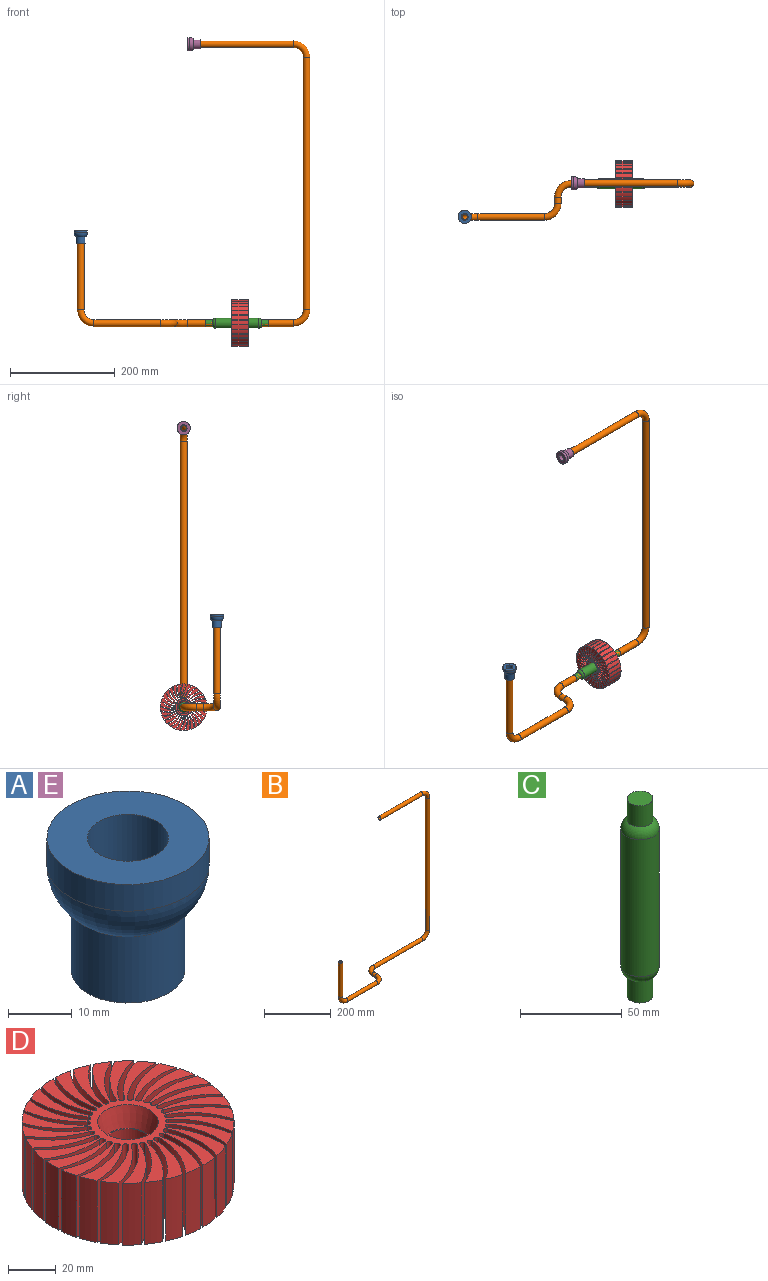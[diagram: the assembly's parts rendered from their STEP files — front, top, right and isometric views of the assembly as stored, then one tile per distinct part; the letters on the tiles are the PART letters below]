
ASSEMBLY  parts=5 mates=4
PART A: 6 faces, bbox 25.4x25.4x25.4 mm
  f0: plane 17.78x17.78mm, normal (0,0,-1), area 121.6mm2, adj f1,f5
  f1: cylinder r=6.35mm len=25.4mm, axis (0,0,-1), area 1013.4mm2, adj f0,f2
  f2: plane 25.4x25.4mm, normal (0,0,1), area 380mm2, adj f1,f3
  f3: cylinder r=12.7mm len=25.4mm, axis (0,0,-1), area 405.4mm2, adj f2,f4
  f4: torus R=3.17mm, axis (0,0,-1), area 632.2mm2, adj f3,f5
  f5: cylinder r=8.89mm len=17.78mm, axis (0,0,-1), area 709.4mm2, adj f0,f4
PART B: 24 faces, bbox 449.7x81.4x551.3 mm
  f0: cylinder r=4.91mm len=127mm, axis (0,0,-1), area 3916.4mm2, adj f1,f11
  f1: torus R=25.4mm, axis (0,-1,0), area 1230.4mm2, adj f0,f2
  f2: cylinder r=4.91mm len=127mm, axis (1,0,0), area 3916.4mm2, adj f1,f3
  f3: torus R=25.4mm, axis (0,0,1), area 1230.4mm2, adj f2,f4
  f4: cylinder r=4.91mm len=12.7mm, axis (0,1,0), area 391.6mm2, adj f3,f5
  f5: torus R=25.4mm, axis (0,0,-1), area 1230.4mm2, adj f4,f6
  f6: cylinder r=4.91mm len=203.2mm, axis (1,0,0), area 6266.3mm2, adj f5,f7
  f7: torus R=25.4mm, axis (0,-1,0), area 1230.4mm2, adj f6,f8
  f8: cylinder r=4.91mm len=482.6mm, axis (0,0,1), area 14882.4mm2, adj f7,f9
  f9: torus R=25.4mm, axis (0,-1,0), area 1230.4mm2, adj f8,f10
  f10: cylinder r=4.91mm len=177.8mm, axis (-1,0,0), area 5483mm2, adj f9,f12
  f11: plane 12.7x12.7mm, normal (0,0,1), area 51mm2, adj f0,f13
  f12: plane 12.7x12.7mm, normal (-1,0,0), area 51mm2, adj f10,f23
  f13: cylinder r=6.35mm len=127mm, axis (0,0,-1), area 5067.1mm2, adj f11,f14
  f14: torus R=25.4mm, axis (0,-1,0), area 1591.9mm2, adj f13,f15
  f15: cylinder r=6.35mm len=127mm, axis (1,0,0), area 5067.1mm2, adj f14,f16
  f16: torus R=25.4mm, axis (0,0,1), area 1591.9mm2, adj f15,f17
  f17: cylinder r=6.35mm len=12.7mm, axis (0,1,0), area 506.7mm2, adj f16,f18
  f18: torus R=25.4mm, axis (0,0,-1), area 1591.9mm2, adj f17,f19
  f19: cylinder r=6.35mm len=203.2mm, axis (1,0,0), area 8107.3mm2, adj f18,f20
  f20: torus R=25.4mm, axis (0,-1,0), area 1591.9mm2, adj f19,f21
  f21: cylinder r=6.35mm len=482.6mm, axis (0,0,1), area 19254.9mm2, adj f20,f22
  f22: torus R=25.4mm, axis (0,-1,0), area 1591.9mm2, adj f21,f23
  f23: cylinder r=6.35mm len=177.8mm, axis (-1,0,0), area 7093.9mm2, adj f12,f22
PART C: 7 faces, bbox 19.1x19.1x118.8 mm
  f0: cylinder r=9.53mm len=82.55mm, axis (0,0,-1), area 4940.4mm2, adj f3,f6
  f1: plane 12.7x12.7mm, normal (0,0,1), area 126.7mm2, adj f2
  f2: cylinder r=6.35mm len=12.7mm, axis (0,0,-1), area 506.7mm2, adj f1,f3
  f3: torus R=3.31mm, axis (0,0,-1), area 348.8mm2, adj f0,f2
  f4: plane 12.7x12.7mm, normal (0,0,-1), area 126.7mm2, adj f5
  f5: cylinder r=6.35mm len=12.7mm, axis (0,0,1), area 506.7mm2, adj f4,f6
  f6: torus R=3.31mm, axis (0,0,1), area 348.8mm2, adj f0,f5
PART D: 125 faces, bbox 88.9x88.9x31.8 mm
  f0: cylinder r=44.45mm len=31.75mm, axis (0,0,-1), area 250.2mm2, adj f1,f117,f118,f124
  f1: cylinder r=38.1mm len=31.75mm, axis (0,0,1), area 922.7mm2, adj f0,f2,f117,f118
  f2: cylinder r=1.27mm len=31.75mm, axis (0,0,1), area 126.7mm2, adj f1,f3,f117,f118
  f3: cylinder r=40.64mm len=31.75mm, axis (0,0,1), area 895.9mm2, adj f2,f4,f117,f118
  f4: cylinder r=44.45mm len=31.75mm, axis (0,0,-1), area 250.2mm2, adj f3,f5,f117,f118
  f5: cylinder r=38.1mm len=31.75mm, axis (0,0,1), area 922.7mm2, adj f4,f6,f117,f118
  f6: cylinder r=1.27mm len=31.75mm, axis (0,0,1), area 126.7mm2, adj f5,f7,f117,f118
  f7: cylinder r=40.64mm len=31.75mm, axis (0,0,1), area 895.9mm2, adj f6,f8,f117,f118
  f8: cylinder r=44.45mm len=31.75mm, axis (0,0,-1), area 250.2mm2, adj f7,f9,f117,f118
  f9: cylinder r=38.1mm len=31.75mm, axis (0,0,1), area 922.7mm2, adj f8,f10,f117,f118
  f10: cylinder r=1.27mm len=31.75mm, axis (0,0,1), area 126.7mm2, adj f9,f11,f117,f118
  f11: cylinder r=40.64mm len=31.75mm, axis (0,0,1), area 895.9mm2, adj f10,f12,f117,f118
  f12: cylinder r=44.45mm len=31.75mm, axis (0,0,-1), area 250.2mm2, adj f11,f13,f117,f118
  f13: cylinder r=38.1mm len=31.75mm, axis (0,0,1), area 922.7mm2, adj f12,f14,f117,f118
  f14: cylinder r=1.27mm len=31.75mm, axis (0,0,1), area 126.7mm2, adj f13,f15,f117,f118
  f15: cylinder r=40.64mm len=31.75mm, axis (0,0,1), area 895.9mm2, adj f14,f16,f117,f118
  f16: cylinder r=44.45mm len=31.75mm, axis (0,0,-1), area 250.2mm2, adj f15,f17,f117,f118
  f17: cylinder r=38.1mm len=31.75mm, axis (0,0,1), area 922.7mm2, adj f16,f18,f117,f118
  f18: cylinder r=1.27mm len=31.75mm, axis (0,0,1), area 126.7mm2, adj f17,f19,f117,f118
  f19: cylinder r=40.64mm len=31.75mm, axis (0,0,1), area 895.9mm2, adj f18,f20,f117,f118
  f20: cylinder r=44.45mm len=31.75mm, axis (0,0,-1), area 250.2mm2, adj f19,f21,f117,f118
  f21: cylinder r=38.1mm len=31.75mm, axis (0,0,1), area 922.7mm2, adj f20,f22,f117,f118
  f22: cylinder r=1.27mm len=31.75mm, axis (0,0,1), area 126.7mm2, adj f21,f23,f117,f118
  f23: cylinder r=40.64mm len=31.75mm, axis (0,0,1), area 895.9mm2, adj f22,f24,f117,f118
  f24: cylinder r=44.45mm len=31.75mm, axis (0,0,-1), area 250.2mm2, adj f23,f25,f117,f118
  f25: cylinder r=38.1mm len=31.75mm, axis (0,0,1), area 922.7mm2, adj f24,f26,f117,f118
  f26: cylinder r=1.27mm len=31.75mm, axis (0,0,1), area 126.7mm2, adj f25,f27,f117,f118
  f27: cylinder r=40.64mm len=31.75mm, axis (0,0,1), area 895.9mm2, adj f26,f28,f117,f118
  f28: cylinder r=44.45mm len=31.75mm, axis (0,0,-1), area 250.2mm2, adj f27,f29,f117,f118
  f29: cylinder r=38.1mm len=31.75mm, axis (0,0,1), area 922.7mm2, adj f28,f30,f117,f118
  f30: cylinder r=1.27mm len=31.75mm, axis (0,0,1), area 126.7mm2, adj f29,f31,f117,f118
  f31: cylinder r=40.64mm len=31.75mm, axis (0,0,1), area 895.9mm2, adj f30,f32,f117,f118
  f32: cylinder r=44.45mm len=31.75mm, axis (0,0,-1), area 250.2mm2, adj f31,f33,f117,f118
  f33: cylinder r=38.1mm len=31.75mm, axis (0,0,1), area 922.7mm2, adj f32,f34,f117,f118
  f34: cylinder r=1.27mm len=31.75mm, axis (0,0,1), area 126.7mm2, adj f33,f35,f117,f118
  f35: cylinder r=40.64mm len=31.75mm, axis (0,0,1), area 895.9mm2, adj f34,f36,f117,f118
  f36: cylinder r=44.45mm len=31.75mm, axis (0,0,-1), area 250.2mm2, adj f35,f37,f117,f118
  f37: cylinder r=38.1mm len=31.75mm, axis (0,0,1), area 922.7mm2, adj f36,f38,f117,f118
  f38: cylinder r=1.27mm len=31.75mm, axis (0,0,1), area 126.7mm2, adj f37,f39,f117,f118
  f39: cylinder r=40.64mm len=31.75mm, axis (0,0,1), area 895.9mm2, adj f38,f40,f117,f118
  f40: cylinder r=44.45mm len=31.75mm, axis (0,0,-1), area 250.2mm2, adj f39,f41,f117,f118
  f41: cylinder r=38.1mm len=31.75mm, axis (0,0,1), area 922.7mm2, adj f40,f42,f117,f118
  f42: cylinder r=1.27mm len=31.75mm, axis (0,0,1), area 126.7mm2, adj f41,f43,f117,f118
  f43: cylinder r=40.64mm len=31.75mm, axis (0,0,1), area 895.9mm2, adj f42,f44,f117,f118
  f44: cylinder r=44.45mm len=31.75mm, axis (0,0,-1), area 250.2mm2, adj f43,f45,f117,f118
  f45: cylinder r=38.1mm len=31.75mm, axis (0,0,1), area 922.7mm2, adj f44,f46,f117,f118
  f46: cylinder r=1.27mm len=31.75mm, axis (0,0,1), area 126.7mm2, adj f45,f47,f117,f118
  f47: cylinder r=40.64mm len=31.75mm, axis (0,0,1), area 895.9mm2, adj f46,f48,f117,f118
  f48: cylinder r=44.45mm len=31.75mm, axis (0,0,-1), area 250.2mm2, adj f47,f49,f117,f118
  f49: cylinder r=38.1mm len=31.75mm, axis (0,0,1), area 922.7mm2, adj f48,f50,f117,f118
  f50: cylinder r=1.27mm len=31.75mm, axis (0,0,1), area 126.7mm2, adj f49,f51,f117,f118
  f51: cylinder r=40.64mm len=31.75mm, axis (0,0,1), area 895.9mm2, adj f50,f52,f117,f118
  f52: cylinder r=44.45mm len=31.75mm, axis (0,0,-1), area 250.2mm2, adj f51,f53,f117,f118
  f53: cylinder r=38.1mm len=31.75mm, axis (0,0,1), area 922.7mm2, adj f52,f54,f117,f118
  f54: cylinder r=1.27mm len=31.75mm, axis (0,0,1), area 126.7mm2, adj f53,f55,f117,f118
  f55: cylinder r=40.64mm len=31.75mm, axis (0,0,1), area 895.9mm2, adj f54,f56,f117,f118
  f56: cylinder r=44.45mm len=31.75mm, axis (0,0,-1), area 250.2mm2, adj f55,f57,f117,f118
  f57: cylinder r=38.1mm len=31.75mm, axis (0,0,1), area 922.7mm2, adj f56,f58,f117,f118
  f58: cylinder r=1.27mm len=31.75mm, axis (0,0,1), area 126.7mm2, adj f57,f59,f117,f118
  f59: cylinder r=40.64mm len=31.75mm, axis (0,0,1), area 895.9mm2, adj f58,f60,f117,f118
  f60: cylinder r=44.45mm len=31.75mm, axis (0,0,-1), area 250.2mm2, adj f59,f61,f117,f118
  f61: cylinder r=38.1mm len=31.75mm, axis (0,0,1), area 922.7mm2, adj f60,f62,f117,f118
  f62: cylinder r=1.27mm len=31.75mm, axis (0,0,1), area 126.7mm2, adj f61,f63,f117,f118
  f63: cylinder r=40.64mm len=31.75mm, axis (0,0,1), area 895.9mm2, adj f62,f64,f117,f118
  f64: cylinder r=44.45mm len=31.75mm, axis (0,0,-1), area 250.2mm2, adj f63,f65,f117,f118
  f65: cylinder r=38.1mm len=31.75mm, axis (0,0,1), area 922.7mm2, adj f64,f66,f117,f118
  f66: cylinder r=1.27mm len=31.75mm, axis (0,0,1), area 126.7mm2, adj f65,f67,f117,f118
  f67: cylinder r=40.64mm len=31.75mm, axis (0,0,1), area 895.9mm2, adj f66,f68,f117,f118
  f68: cylinder r=44.45mm len=31.75mm, axis (0,0,-1), area 250.2mm2, adj f67,f69,f117,f118
  f69: cylinder r=38.1mm len=31.75mm, axis (0,0,1), area 922.7mm2, adj f68,f70,f117,f118
  f70: cylinder r=1.27mm len=31.75mm, axis (0,0,1), area 126.7mm2, adj f69,f71,f117,f118
  f71: cylinder r=40.64mm len=31.75mm, axis (0,0,1), area 895.9mm2, adj f70,f72,f117,f118
  f72: cylinder r=44.45mm len=31.75mm, axis (0,0,-1), area 250.2mm2, adj f71,f73,f117,f118
  f73: cylinder r=38.1mm len=31.75mm, axis (0,0,1), area 922.7mm2, adj f72,f74,f117,f118
  f74: cylinder r=1.27mm len=31.75mm, axis (0,0,1), area 126.7mm2, adj f73,f75,f117,f118
  f75: cylinder r=40.64mm len=31.75mm, axis (0,0,1), area 895.9mm2, adj f74,f76,f117,f118
  f76: cylinder r=44.45mm len=31.75mm, axis (0,0,-1), area 250.2mm2, adj f75,f77,f117,f118
  f77: cylinder r=38.1mm len=31.75mm, axis (0,0,1), area 922.7mm2, adj f76,f78,f117,f118
  f78: cylinder r=1.27mm len=31.75mm, axis (0,0,1), area 126.7mm2, adj f77,f79,f117,f118
  f79: cylinder r=40.64mm len=31.75mm, axis (0,0,1), area 895.9mm2, adj f78,f80,f117,f118
  f80: cylinder r=44.45mm len=31.75mm, axis (0,0,-1), area 250.2mm2, adj f79,f81,f117,f118
  f81: cylinder r=38.1mm len=31.75mm, axis (0,0,1), area 922.7mm2, adj f80,f82,f117,f118
  f82: cylinder r=1.27mm len=31.75mm, axis (0,0,1), area 126.7mm2, adj f81,f83,f117,f118
  f83: cylinder r=40.64mm len=31.75mm, axis (0,0,1), area 895.9mm2, adj f82,f84,f117,f118
  f84: cylinder r=44.45mm len=31.75mm, axis (0,0,-1), area 250.2mm2, adj f83,f85,f117,f118
  f85: cylinder r=38.1mm len=31.75mm, axis (0,0,1), area 922.7mm2, adj f84,f86,f117,f118
  f86: cylinder r=1.27mm len=31.75mm, axis (0,0,1), area 126.7mm2, adj f85,f87,f117,f118
  f87: cylinder r=40.64mm len=31.75mm, axis (0,0,1), area 895.9mm2, adj f86,f88,f117,f118
  f88: cylinder r=44.45mm len=31.75mm, axis (0,0,-1), area 250.2mm2, adj f87,f89,f117,f118
  f89: cylinder r=38.1mm len=31.75mm, axis (0,0,1), area 922.7mm2, adj f88,f90,f117,f118
  f90: cylinder r=1.27mm len=31.75mm, axis (0,0,1), area 126.7mm2, adj f89,f91,f117,f118
  f91: cylinder r=40.64mm len=31.75mm, axis (0,0,1), area 895.9mm2, adj f90,f92,f117,f118
  f92: cylinder r=44.45mm len=31.75mm, axis (0,0,-1), area 250.2mm2, adj f91,f93,f117,f118
  f93: cylinder r=38.1mm len=31.75mm, axis (0,0,1), area 922.7mm2, adj f92,f94,f117,f118
  f94: cylinder r=1.27mm len=31.75mm, axis (0,0,1), area 126.7mm2, adj f93,f95,f117,f118
  f95: cylinder r=40.64mm len=31.75mm, axis (0,0,1), area 895.9mm2, adj f94,f96,f117,f118
  f96: cylinder r=44.45mm len=31.75mm, axis (0,0,-1), area 250.2mm2, adj f95,f97,f117,f118
  f97: cylinder r=38.1mm len=31.75mm, axis (0,0,1), area 922.7mm2, adj f96,f98,f117,f118
  f98: cylinder r=1.27mm len=31.75mm, axis (0,0,1), area 126.7mm2, adj f97,f99,f117,f118
  f99: cylinder r=40.64mm len=31.75mm, axis (0,0,1), area 895.9mm2, adj f98,f100,f117,f118
  f100: cylinder r=44.45mm len=31.75mm, axis (0,0,-1), area 250.2mm2, adj f99,f101,f117,f118
  f101: cylinder r=38.1mm len=31.75mm, axis (0,0,1), area 922.7mm2, adj f100,f102,f117,f118
  f102: cylinder r=1.27mm len=31.75mm, axis (0,0,1), area 126.7mm2, adj f101,f103,f117,f118
  f103: cylinder r=40.64mm len=31.75mm, axis (0,0,1), area 895.9mm2, adj f102,f104,f117,f118
  f104: cylinder r=44.45mm len=31.75mm, axis (0,0,-1), area 250.2mm2, adj f103,f105,f117,f118
  f105: cylinder r=38.1mm len=31.75mm, axis (0,0,1), area 922.7mm2, adj f104,f106,f117,f118
  f106: cylinder r=1.27mm len=31.75mm, axis (0,0,1), area 126.7mm2, adj f105,f107,f117,f118
  f107: cylinder r=40.64mm len=31.75mm, axis (0,0,1), area 895.9mm2, adj f106,f108,f117,f118
  f108: cylinder r=44.45mm len=31.75mm, axis (0,0,-1), area 250.2mm2, adj f107,f109,f117,f118
  f109: cylinder r=38.1mm len=31.75mm, axis (0,0,1), area 922.7mm2, adj f108,f110,f117,f118
  f110: cylinder r=1.27mm len=31.75mm, axis (0,0,1), area 126.7mm2, adj f109,f111,f117,f118
  f111: cylinder r=40.64mm len=31.75mm, axis (0,0,1), area 895.9mm2, adj f110,f112,f117,f118
  f112: cylinder r=44.45mm len=31.75mm, axis (0,0,-1), area 250.2mm2, adj f111,f113,f117,f118
  f113: cylinder r=38.1mm len=31.75mm, axis (0,0,1), area 922.7mm2, adj f112,f114,f117,f118
  f114: cylinder r=1.27mm len=31.75mm, axis (0,0,1), area 126.7mm2, adj f113,f115,f117,f118
  f115: cylinder r=40.64mm len=31.75mm, axis (0,0,1), area 895.9mm2, adj f114,f116,f117,f118
  f116: cylinder r=44.45mm len=31.75mm, axis (0,0,-1), area 250.2mm2, adj f115,f117,f118,f122
  f117: plane 88.9x88.9mm, normal (0,0,1), area 3818mm2, adj f0,f1,f2,f3,f4,f5,f6,f7
  f118: plane 88.9x88.9mm, normal (0,0,-1), area 4039.7mm2, adj f0,f1,f2,f3,f4,f5,f6,f7
  f119: cone r=12.7mm half-angle=15deg, axis (0,0,1), area 749.4mm2, adj f117,f120
  f120: plane 19.96x19.96mm, normal (0,0,1), area 27.7mm2, adj f119,f121
  f121: cylinder r=9.53mm len=21.59mm, axis (0,0,1), area 1292.1mm2, adj f118,f120
  f122: cylinder r=38.1mm len=31.75mm, axis (0,0,1), area 922.7mm2, adj f116,f117,f118,f123
  f123: cylinder r=1.27mm len=31.75mm, axis (0,0,1), area 126.7mm2, adj f117,f118,f122,f124
  f124: cylinder r=40.64mm len=31.75mm, axis (0,0,1), area 895.9mm2, adj f0,f117,f118,f123
PART E: same geometry as A
PLACE A t=(-110.45,67.49,-56.76)mm
PLACE B t=(-110.45,67.49,-56.76)mm fixed
PLACE C rot(axis=(0,1,0),90deg) t=(172.5,130.99,-209.16)mm
PLACE D rot(axis=(-0.67,-0.32,0.67),145deg) t=(209.97,130.99,-209.16)mm
PLACE E rot(axis=(0,-1,0),90deg) t=(118.15,130.99,324.24)mm
MATE slider C.f0 <-> B.f6  axis (-1,0,0) through (128.98,130.99,-209.16)mm
MATE revolute D.f119 <-> C.f0  axis (-1,0,0) through (188.38,130.99,-209.16)mm
MATE fastened A.f1 <-> B.f0  axis (0,0,-1) through (-110.45,67.49,-56.76)mm
MATE fastened B.f10 <-> E.f1  axis (-1,0,0) through (118.15,130.99,324.24)mm
